# Revit family: Gira_541000
name_source: partatom
category: Electrical Fixtures
revit_build: Autodesk Revit 2017 (Build: 20160225_1515(x64)
units: mm (PartAtom-declared; Revit-internal decimal feet)

## family parameters
Cut with Voids When Loaded = No
Host = Face
Maintain Annotation Orientation = Yes
Part Type = Normal
Room Calculation Point = No
Round Connector Dimension = Use Diameter
Shared = No

## types (1)
- S3000 Impulseins. Einsatz
    Available = Yes
    Category = Bewegungsmelder Basiselement
    Data sheet (1) = https://katalog.gira.de
    Default Elevation = 1219 mm
    Eingang für Nebenstelle = No
    GTIN = 4010337048305
    Geeignet für 230 V Glühlampe/Halogenlampe = Yes
    Geeignet für Leuchtstofflampe/Energiesparlampe = Yes
    Geeignet für Schutzart (IP) = IP20
    Geeignet für Treppenlichtzeitschalter = No
    Geeignet für elektronischen Niedervolttrafo = Yes
    Geeignet für gewickelten Niedervolttrafo = Yes
    HAN = 541000
    HeinzeBIM = https://bimportal.heinze.de
    Keynote = Einsatz_1fach
    Manufacturer URL = https://www.gira.de
    Min. Tiefe der Gerätedose = 0,024 m
    Mit N-Leiter = No
    Montageart = unter Putz
    Name = S3000 Impulseins. Einsatz
    Nennspannung = 230 Volt
    Nur geeignet als Nebenstelle = No
    Region = DE
    Temperatur = 5 - 45
    URL = http://katalog.gira.de
    Zwangsabschaltung = No

## geometry (parser evidence)
native form markers: Blend x2, Sweep x3
no freeform markers — native parametric forms only
